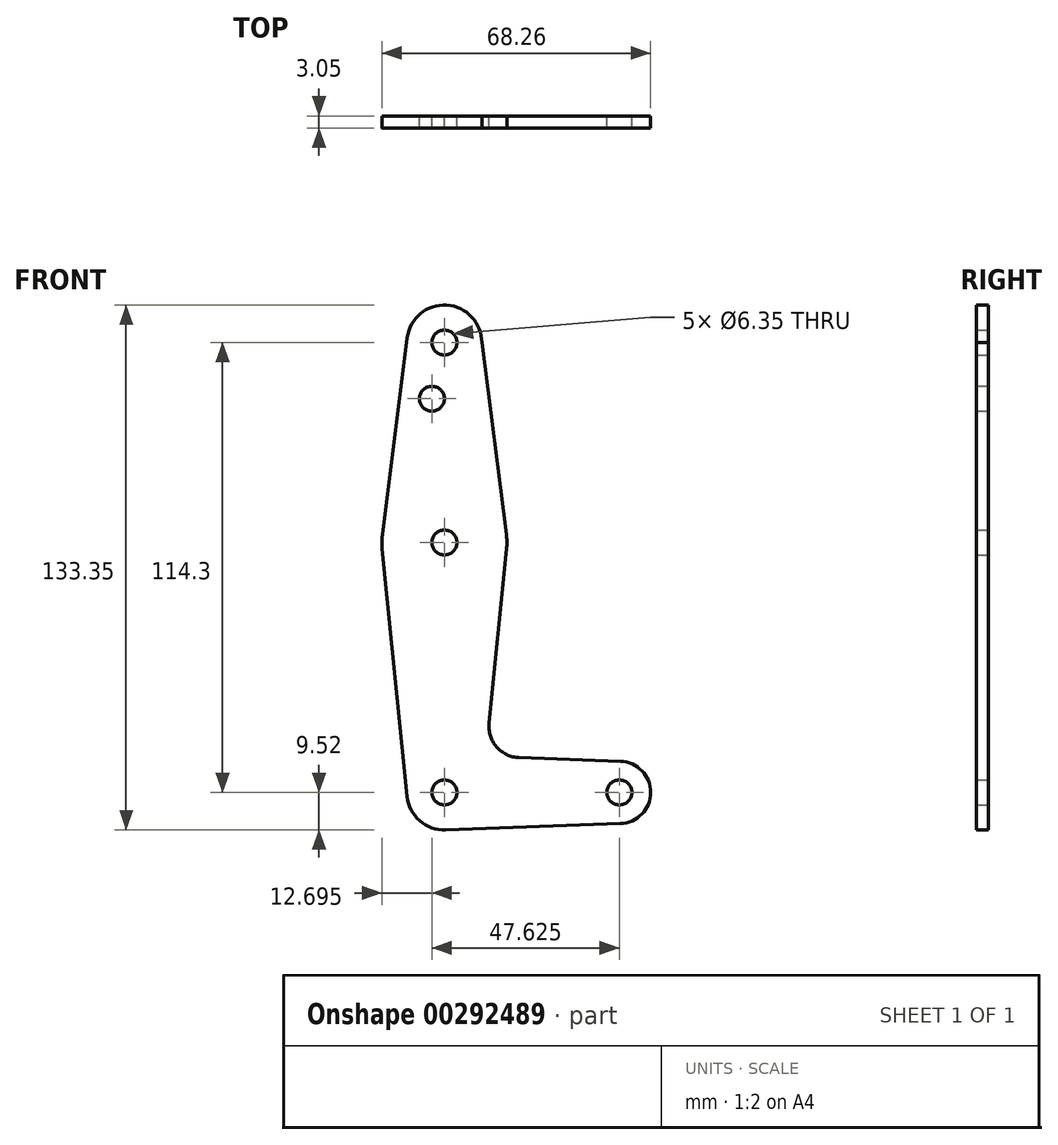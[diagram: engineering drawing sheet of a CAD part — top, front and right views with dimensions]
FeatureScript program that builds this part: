
annotation { "Feature Type Name" : "Feature", "Feature Type Description" : "" }
export const myFeature = defineFeature(function(context is Context, id is Id, definition is map)
    precondition{}
    {
        {
            var Q0;
            Q0=qCreatedBy(makeId("Front.planeOp"),FACE);
            var sketch = newSketch(context, id + "F0", { "sketchPlane" : qUnion([Q0])});
            skLineSegment(sketch, "E0", {"start": v(0, 0) * mm, "end": v(0, 114.3) * mm, "construction": true});
            skLineSegment(sketch, "E1", {"start": v(0, 0) * mm, "end": v(44.45, 0) * mm, "construction": true});
            skCircle(sketch, "E2", {"center": v(0, 114.3) * mm, "radius": 9.53 * mm});
            skCircle(sketch, "E3", {"center": v(0, 63.5) * mm, "radius": 15.88 * mm});
            skCircle(sketch, "E4", {"center": v(0, 0) * mm, "radius": 9.53 * mm});
            skCircle(sketch, "E5", {"center": v(44.45, 0) * mm, "radius": 7.94 * mm});
            skLineSegment(sketch, "E6", {"start": v(-9.45, 115.5) * mm, "end": v(-15.75, 65.48) * mm});
            skLineSegment(sketch, "E7", {"start": v(9.53, 114.3) * mm, "end": v(15.75, 65.5) * mm});
            skLineSegment(sketch, "E8", {"start": v(-15.8, 61.91) * mm, "end": v(-9.48, -0.95) * mm});
            skLineSegment(sketch, "E9", {"start": v(15.8, 61.91) * mm, "end": v(11.34, 17.6) * mm});
            skLineSegment(sketch, "E10", {"start": v(18.97, 8.85) * mm, "end": v(44.73, 7.93) * mm});
            skLineSegment(sketch, "E11", {"start": v(0.34, -9.52) * mm, "end": v(44.73, -7.93) * mm});
            skCircle(sketch, "E12", {"center": v(0, 114.3) * mm, "radius": 3.18 * mm});
            skCircle(sketch, "E13", {"center": v(0, 63.5) * mm, "radius": 3.18 * mm});
            skCircle(sketch, "E14", {"center": v(0, 0) * mm, "radius": 3.18 * mm});
            skCircle(sketch, "E15", {"center": v(44.45, 0) * mm, "radius": 3.18 * mm});
            skCircle(sketch, "E16", {"center": v(-3.18, 100.03) * mm, "radius": 3.18 * mm});
            skArc(sketch, "E17.filletArc", {"start": v(11.34, 17.6) * mm, "mid": v(13.26, 11.57) * mm, "end": v(18.97, 8.85) * mm});
            skSolve(sketch);
        }
        {
            var Q0;
            Q0=qSketchRegion(id+"F0",true);
            extrude(context, id + "F1", {"entities" : qUnion([Q0]), "depth" : 3.05 * mm});
        }
    });
